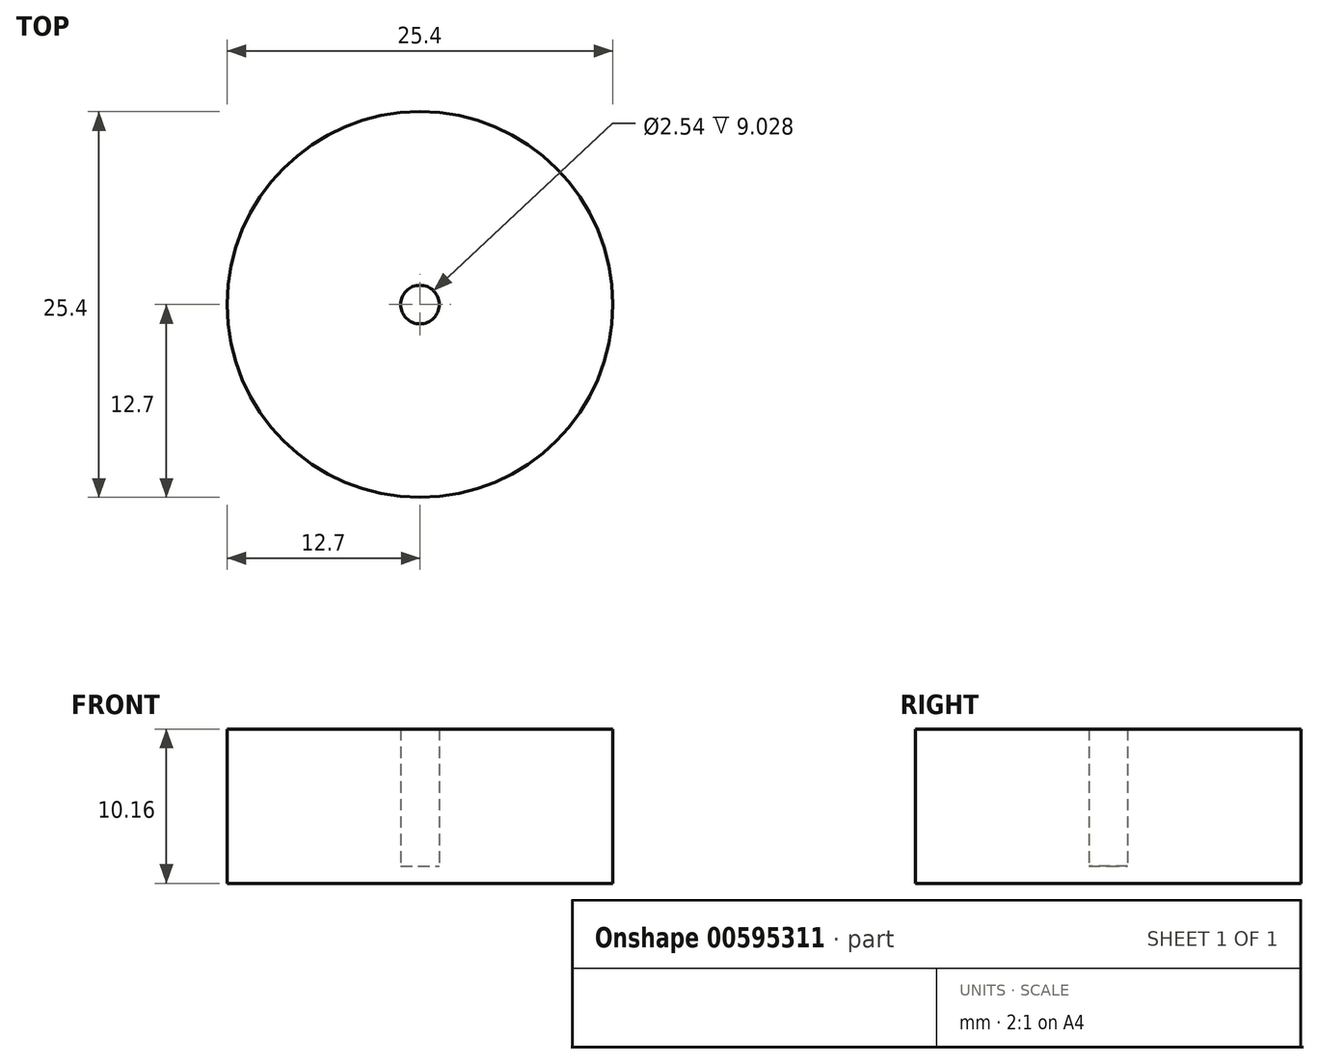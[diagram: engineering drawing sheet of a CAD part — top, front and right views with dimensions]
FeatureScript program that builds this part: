
annotation { "Feature Type Name" : "Feature", "Feature Type Description" : "" }
export const myFeature = defineFeature(function(context is Context, id is Id, definition is map)
    precondition{}
    {
        {
            var Q0;
            Q0=qCreatedBy(makeId("Front.planeOp"),FACE);
            var sketch = newSketch(context, id + "F0", { "sketchPlane" : qUnion([Q0])});
            skLineSegment(sketch, "E0", {"start": v(0, 0) * mm, "end": v(-1.27, 0) * mm});
            skLineSegment(sketch, "E1", {"start": v(-1.27, 10.16) * mm, "end": v(-12.7, 10.16) * mm});
            skLineSegment(sketch, "E2", {"start": v(-12.7, 10.16) * mm, "end": v(-12.7, 0) * mm});
            skLineSegment(sketch, "E3", {"start": v(-12.7, 0) * mm, "end": v(0, 0) * mm});
            skLineSegment(sketch, "E4", {"start": v(0, 0) * mm, "end": v(0, 1.13) * mm});
            skLineSegment(sketch, "E5", {"start": v(0, 1.13) * mm, "end": v(-1.27, 1.13) * mm});
            skLineSegment(sketch, "E6", {"start": v(-1.27, 1.13) * mm, "end": v(-1.27, 10.16) * mm});
            skSolve(sketch);
        }
        {
            var Q0;
            Q0=makeQuery(id+"F0.imprint","IMPRINT",FACE,{"disambiguationData":[TD([[makeQuery(id+"F0.imprint","IMPRINT",EDGE,{"derivedFrom":sQuery(id+"F0.wireOp",EDGE,"E1")}),1.0]])]});
            var Q1;
            Q1=sQuery(id+"F0.wireOp",EDGE,"E4");
            revolve(context, id + "F1", {"entities" : qUnion([Q0]), "axis" : qUnion([Q1]), "revolveType" : RevolveType.FULL});
        }
    });
